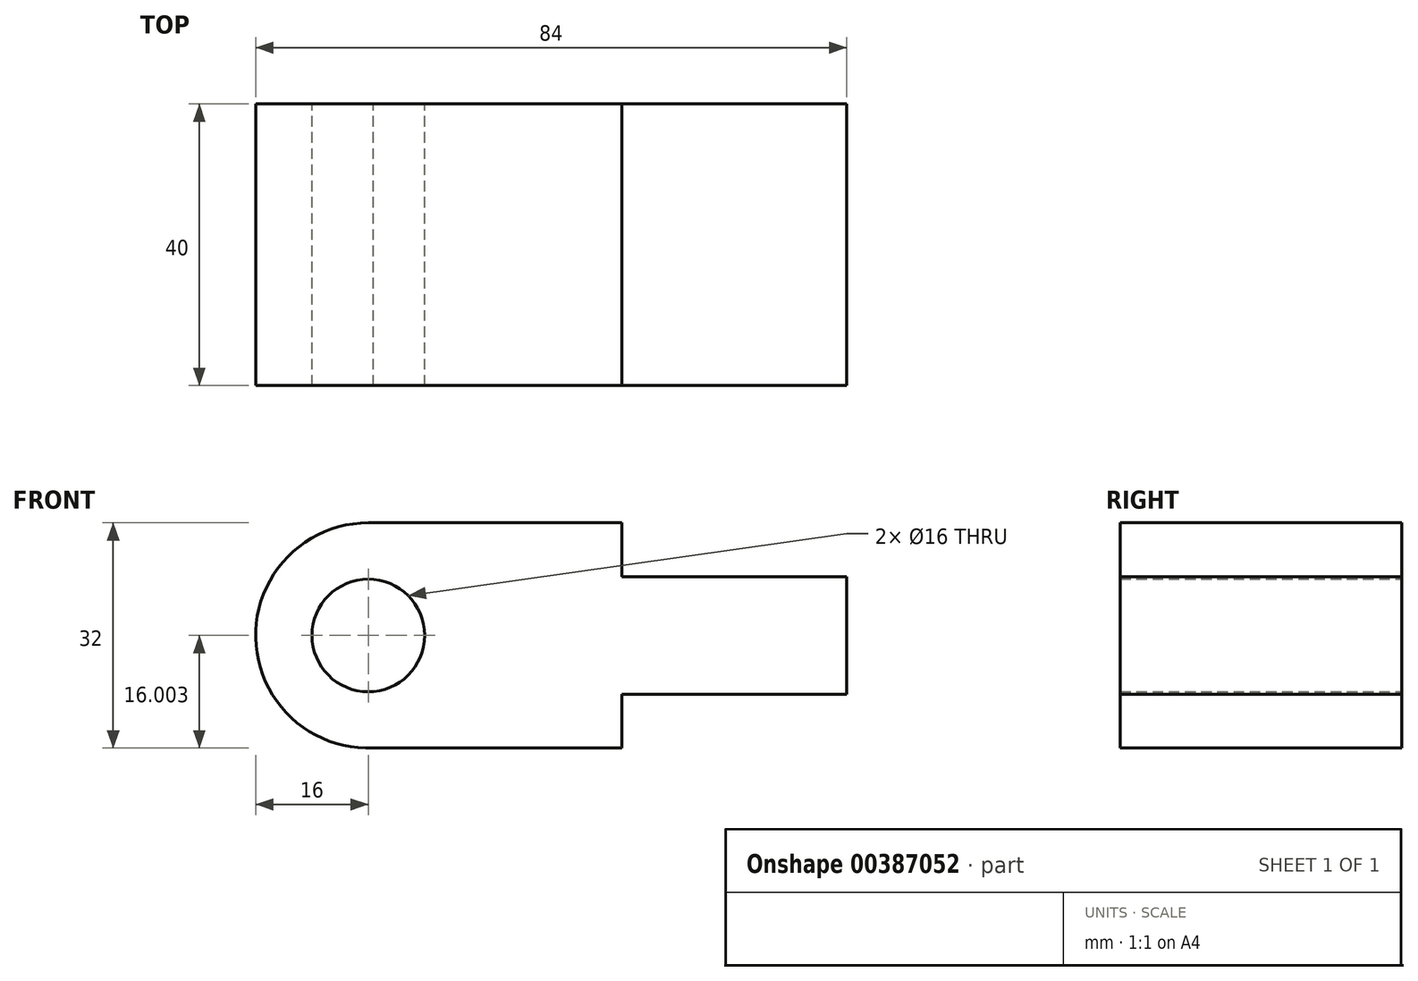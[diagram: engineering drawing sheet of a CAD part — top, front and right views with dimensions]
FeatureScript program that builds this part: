
annotation { "Feature Type Name" : "Feature", "Feature Type Description" : "" }
export const myFeature = defineFeature(function(context is Context, id is Id, definition is map)
    precondition{}
    {
        {
            var Q0;
            Q0=qCreatedBy(makeId("Front.planeOp"),FACE);
            var sketch = newSketch(context, id + "F0", { "sketchPlane" : qUnion([Q0])});
            skLineSegment(sketch, "E0", {"start": v(-30.77, 20.88) * mm, "end": v(5.23, 20.88) * mm});
            skLineSegment(sketch, "E1", {"start": v(5.23, 20.88) * mm, "end": v(5.23, 13.25) * mm});
            skLineSegment(sketch, "E2", {"start": v(5.23, 13.25) * mm, "end": v(37.23, 13.25) * mm});
            skLineSegment(sketch, "E3", {"start": v(37.23, 13.25) * mm, "end": v(37.23, -3.46) * mm});
            skLineSegment(sketch, "E4", {"start": v(37.23, -3.46) * mm, "end": v(5.23, -3.46) * mm});
            skLineSegment(sketch, "E5", {"start": v(5.23, -3.46) * mm, "end": v(5.23, -11.1) * mm});
            skLineSegment(sketch, "E6", {"start": v(5.23, -11.1) * mm, "end": v(-30.05, -11.1) * mm});
            skArc(sketch, "E7", {"start": v(-30.77, 20.88) * mm, "mid": v(-46.77, 4.52) * mm, "end": v(-30.05, -11.1) * mm});
            skCircle(sketch, "E8", {"center": v(-30.77, 4.88) * mm, "radius": 8 * mm});
            skSolve(sketch);
        }
        {
            var Q0;
            Q0=makeQuery(id+"F0.imprint","IMPRINT",FACE,{"disambiguationData":[TD([[makeQuery(id+"F0.imprint","IMPRINT",EDGE,{"derivedFrom":sQuery(id+"F0.wireOp",EDGE,"E0")}),-1.0]])]});
            extrude(context, id + "F1", {"entities" : qUnion([Q0]), "endBound" : BoundingType.SYMMETRIC, "depth" : 40 * mm});
        }
    });
